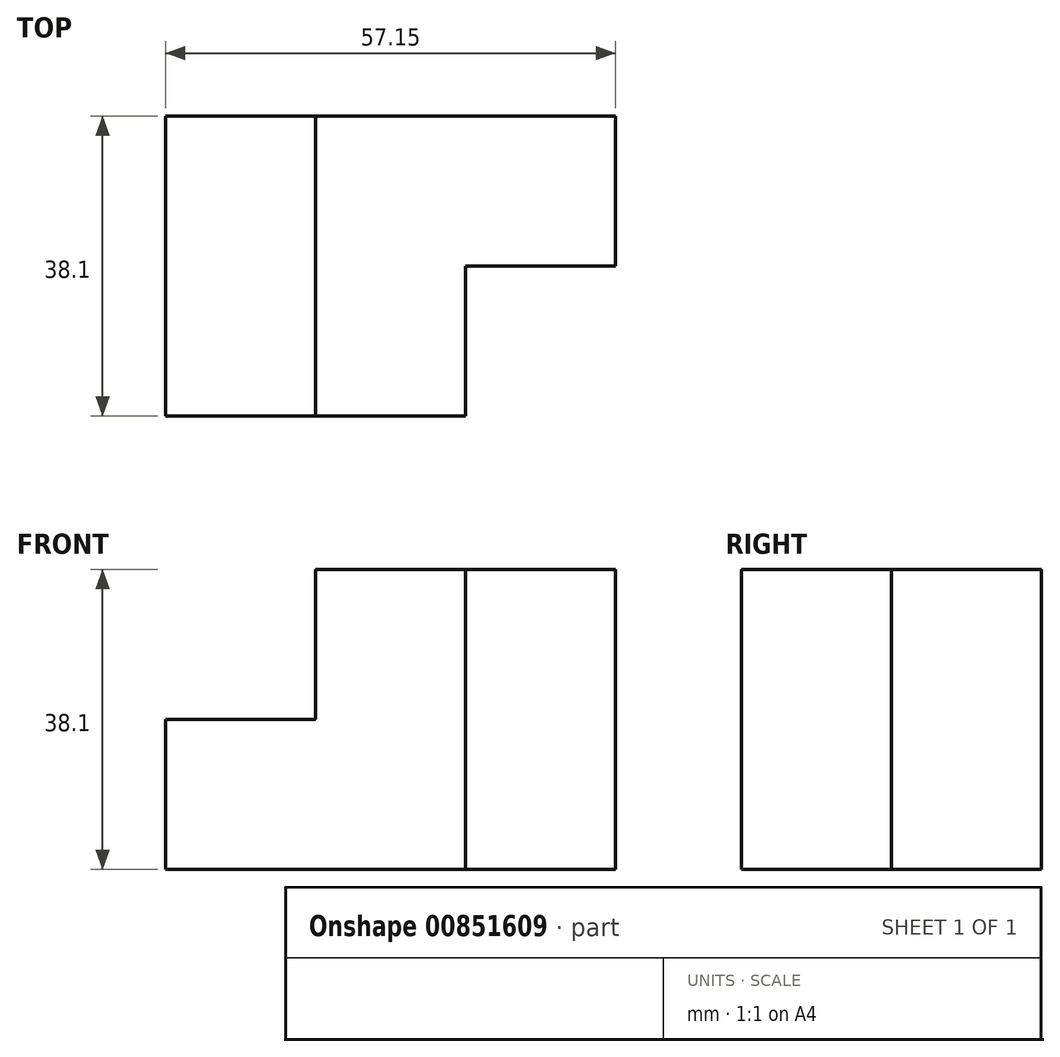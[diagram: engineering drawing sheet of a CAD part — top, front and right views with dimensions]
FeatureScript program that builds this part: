
annotation { "Feature Type Name" : "Feature", "Feature Type Description" : "" }
export const myFeature = defineFeature(function(context is Context, id is Id, definition is map)
    precondition{}
    {
        {
            var Q0;
            Q0=qCreatedBy(makeId("Top.planeOp"),FACE);
            var sketch = newSketch(context, id + "F0", { "sketchPlane" : qUnion([Q0])});
            skLineSegment(sketch, "E0.bottom", {"start": v(19.05, 19.05) * mm, "end": v(-19.05, 19.05) * mm});
            skLineSegment(sketch, "E0.top", {"start": v(19.05, -19.05) * mm, "end": v(-19.05, -19.05) * mm});
            skLineSegment(sketch, "E0.left", {"start": v(19.05, 19.05) * mm, "end": v(19.05, -19.05) * mm});
            skLineSegment(sketch, "E0.right", {"start": v(-19.05, 19.05) * mm, "end": v(-19.05, -19.05) * mm});
            skPoint(sketch, "E0.middle", {"position": v(0, 0) * mm});
            skLineSegment(sketch, "E1", {"start": v(19.05, 19.05) * mm, "end": v(38.1, 19.05) * mm});
            skLineSegment(sketch, "E2", {"start": v(38.1, 19.05) * mm, "end": v(38.1, 0) * mm});
            skLineSegment(sketch, "E3", {"start": v(38.1, 0) * mm, "end": v(19.05, 0) * mm});
            skLineSegment(sketch, "E4", {"start": v(0, 0) * mm, "end": v(0, 19.05) * mm});
            skLineSegment(sketch, "E5", {"start": v(0, 0) * mm, "end": v(19.05, 0) * mm});
            skLineSegment(sketch, "E6", {"start": v(0, 0) * mm, "end": v(0, -19.05) * mm});
            skSolve(sketch);
        }
        {
            var Q0;
            {var subQ3=sQuery(id+"F0.wireOp",EDGE,"E4");Q0=makeQuery(id+"F0.imprint","IMPRINT",FACE,{"disambiguationData":[TD([[makeQuery(id+"F0.imprint","IMPRINT",EDGE,{"derivedFrom":subQ3}),-1.0]])]});}
            var Q1;
            {var subQ0=sQuery(id+"F0.wireOp",EDGE,"E1");Q1=makeQuery(id+"F0.imprint","IMPRINT",FACE,{"disambiguationData":[TD([[makeQuery(id+"F0.imprint","IMPRINT",EDGE,{"derivedFrom":subQ0}),-1.0]])]});}
            var Q2;
            {var subQ4=sQuery(id+"F0.wireOp",EDGE,"E5");Q2=makeQuery(id+"F0.imprint","IMPRINT",FACE,{"disambiguationData":[TD([[makeQuery(id+"F0.imprint","IMPRINT",EDGE,{"derivedFrom":subQ4}),-1.0]])]});}
            extrude(context, id + "F1", {"entities" : qUnion([Q0, Q1, Q2]), "depth" : 38.1 * mm, "offsetDistance" : 25.4 * mm});
        }
        {
            var Q0;
            {var subQ1=sQuery(id+"F0.wireOp",EDGE,"E0.right");Q0=makeQuery(id+"F0.imprint","IMPRINT",FACE,{"disambiguationData":[TD([[makeQuery(id+"F0.imprint","IMPRINT",EDGE,{"derivedFrom":subQ1}),1.0]])]});}
            extrude(context, id + "F2", {"entities" : qUnion([Q0]), "operationType" : NewBodyOperationType.ADD, "depth" : 19.05 * mm, "offsetDistance" : 25.4 * mm});
        }
    });
